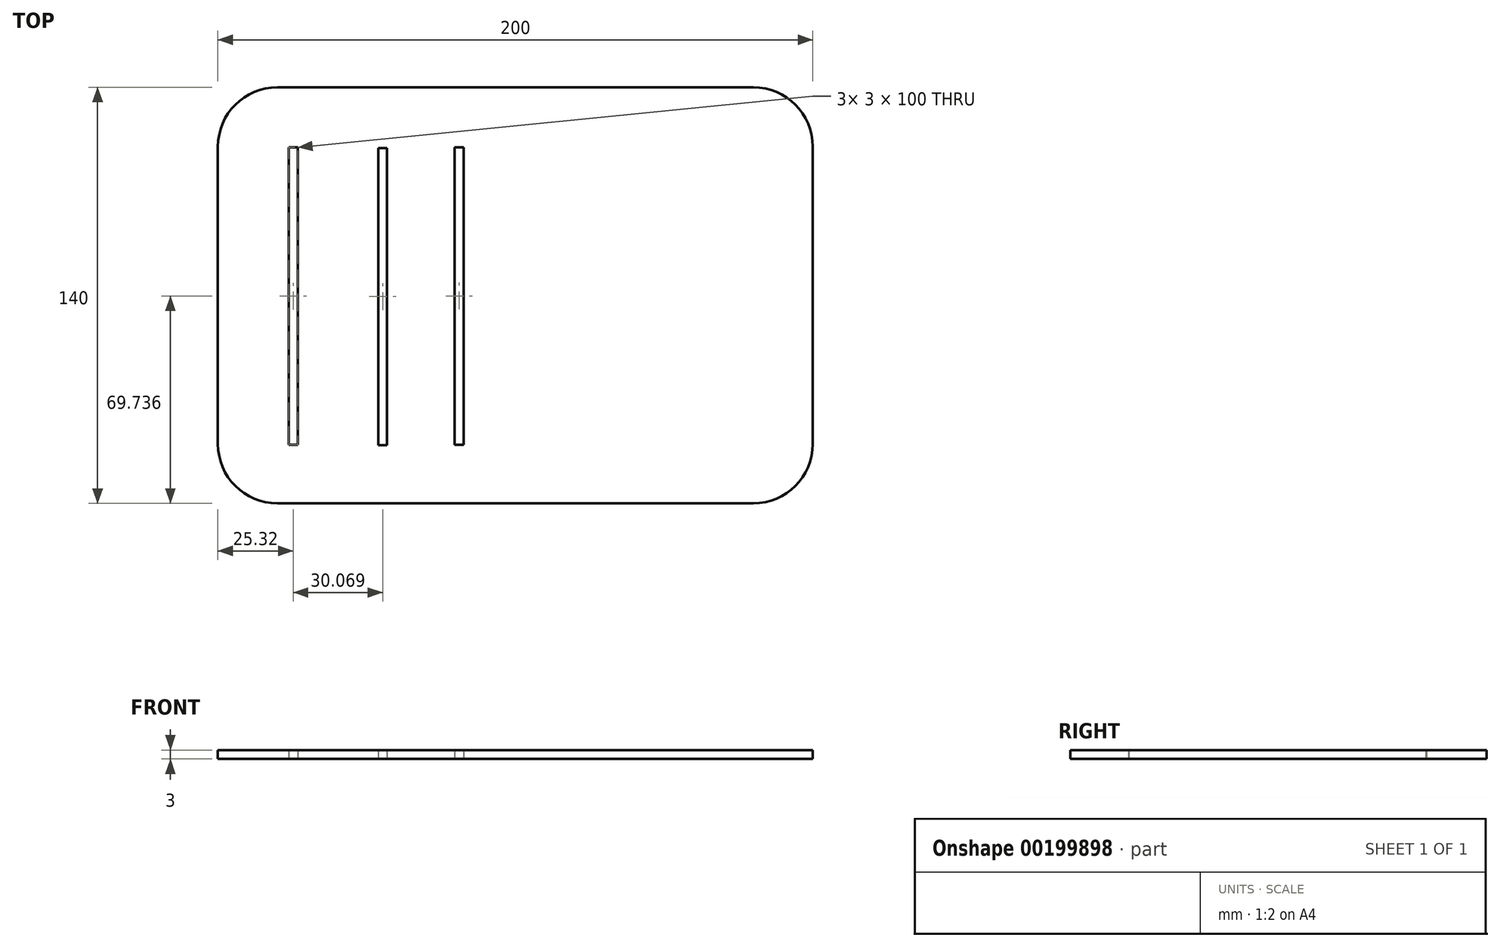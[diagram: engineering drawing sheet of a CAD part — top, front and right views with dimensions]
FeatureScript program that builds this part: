
annotation { "Feature Type Name" : "Feature", "Feature Type Description" : "" }
export const myFeature = defineFeature(function(context is Context, id is Id, definition is map)
    precondition{}
    {
        {
            var Q0;
            Q0=qCreatedBy(makeId("Top.planeOp"),FACE);
            var sketch = newSketch(context, id + "F0", { "sketchPlane" : qUnion([Q0])});
            skLineSegment(sketch, "E0.bottom", {"start": v(80, -70) * mm, "end": v(-80, -70) * mm});
            skLineSegment(sketch, "E0.top", {"start": v(80, 70) * mm, "end": v(-80, 70) * mm});
            skLineSegment(sketch, "E0.left", {"start": v(100, -50) * mm, "end": v(100, 50) * mm});
            skLineSegment(sketch, "E0.right", {"start": v(-100, -50) * mm, "end": v(-100, 50) * mm});
            skPoint(sketch, "E0.middle", {"position": v(0, 0) * mm});
            skPoint(sketch, "E1.visualSharp", {"position": v(100, 70) * mm});
            skArc(sketch, "E1.filletArc", {"start": v(100, 50) * mm, "mid": v(94.14, 64.14) * mm, "end": v(80, 70) * mm});
            skPoint(sketch, "E2.visualSharp", {"position": v(-100, 70) * mm});
            skArc(sketch, "E2.filletArc", {"start": v(-80, 70) * mm, "mid": v(-94.14, 64.14) * mm, "end": v(-100, 50) * mm});
            skPoint(sketch, "E3.visualSharp", {"position": v(-100, -70) * mm});
            skArc(sketch, "E3.filletArc", {"start": v(-100, -50) * mm, "mid": v(-94.14, -64.14) * mm, "end": v(-80, -70) * mm});
            skPoint(sketch, "E4.visualSharp", {"position": v(100, -70) * mm});
            skArc(sketch, "E4.filletArc", {"start": v(80, -70) * mm, "mid": v(94.14, -64.14) * mm, "end": v(100, -50) * mm});
            skLineSegment(sketch, "E5.bottom", {"start": v(-76.18, 49.74) * mm, "end": v(-73.18, 49.74) * mm});
            skLineSegment(sketch, "E5.top", {"start": v(-76.18, -50.26) * mm, "end": v(-73.18, -50.26) * mm});
            skLineSegment(sketch, "E5.left", {"start": v(-76.18, 49.74) * mm, "end": v(-76.18, -50.26) * mm});
            skLineSegment(sketch, "E5.right", {"start": v(-73.18, 49.74) * mm, "end": v(-73.18, -50.26) * mm});
            skLineSegment(sketch, "E6.bottom", {"start": v(-20.41, 49.76) * mm, "end": v(-17.41, 49.76) * mm});
            skLineSegment(sketch, "E6.top", {"start": v(-20.41, -50.24) * mm, "end": v(-17.41, -50.24) * mm});
            skLineSegment(sketch, "E6.left", {"start": v(-20.41, 49.76) * mm, "end": v(-20.41, -50.24) * mm});
            skLineSegment(sketch, "E6.right", {"start": v(-17.41, 49.76) * mm, "end": v(-17.41, -50.24) * mm});
            skLineSegment(sketch, "E7.bottom", {"start": v(-46.11, 49.56) * mm, "end": v(-43.11, 49.56) * mm});
            skLineSegment(sketch, "E7.top", {"start": v(-46.11, -50.44) * mm, "end": v(-43.11, -50.44) * mm});
            skLineSegment(sketch, "E7.left", {"start": v(-46.11, 49.56) * mm, "end": v(-46.11, -50.44) * mm});
            skLineSegment(sketch, "E7.right", {"start": v(-43.11, 49.56) * mm, "end": v(-43.11, -50.44) * mm});
            skLineSegment(sketch, "E8", {"start": v(-73.18, 49.74) * mm, "end": v(38.6, 49.74) * mm, "construction": true});
            skSolve(sketch);
        }
        {
            var Q0;
            Q0 = qSketchRegion(id + "F0", true);
            extrude(context, id + "F1", {"entities" : qUnion([Q0]), "depth" : 3 * mm});
        }
    });
